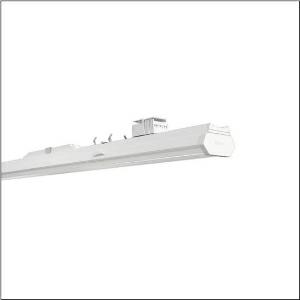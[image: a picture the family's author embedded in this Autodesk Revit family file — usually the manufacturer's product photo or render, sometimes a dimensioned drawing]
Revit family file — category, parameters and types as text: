
# Revit family: licross_r__21_protected_ho_52tp11dn4axs_b31d
name_source: partatom
category: Lighting Fixtures
units: mm (PartAtom-declared; Revit-internal decimal feet)

## family parameters
Cut with Voids When Loaded = No
Host = Face
Light Source = No
Part Type = Normal
Room Calculation Point = No
Round Connector Dimension = Use Diameter
Shared = No

## types (1)
- --- (1 x LED, 10000 lm, 55.1 W, 4000K)
    Apparent Load = 55 VA
    CIE Flux Codes = 84 94 98 99 100
    Color Rendering = 80
    Color Temperature = 4000K
    Default Elevation = 1800 mm
    Description = Licross® 21 Protected HO, luminaire insert, of sheet steel, galvanised, coil coated, white, length: 1.500mm, width: 90mm, height: 103mm, LED rated luminous flux: 10.000lm, light colour: 840, control gear: DALI 2, with plug, 5-pole, with phase selection, mains connection: 220..240V, AC, 50/60Hz, rated input power: 55W, internal wiring halogen-free, primary light control with lens, of plastic, primary optical cover: cover, of PMMA, light emission: direct distribution, primary light characteristic: symmetric, protection rating (complete): IP64, insulation class (complete): insulation class I (protective earthing), certification: CE, ENEC, VDE, UKCA, protection symbol: D if used in an environment with conductive dust loads with corresponding accessories, impact resistance: IK06, permissible ambient temperature for indoor applications: -25..+45°C, corresponds to IFS (International Featured Standards) requirements for safety and quality in the food industry, reducing of maximum allowable ambient temperature of 5°C with ceiling mounting, LABS conformity tested according to VDMA 24364:2018-05, packaging unit: 1 piece
    Height = 92 mm
    Lamp = 1 x LED
    Lamp Light Flux = 10000 lm
    Lamp Power = 55.1 W
    Lamp count = 1
    Length = 1500 mm
    Luminous efficacy = 181 lm/W
    Manufacturer = Siteco
    ModVariant = No
    Model = 52TP11DN4AXS
    Mounting Place = Ceiling
    Mounting Type = Pendant
    Number of Poles = 1
    OnlyDefault = Yes
    Power Factor = 1
    Product Name = Licross® 21 Protected HO
    Product group = luminaire insert | ceiling pendant
    ProductGroupID = 902
    Protection Class = Protection class I
    Protection Degree = IP 64
    RLX_Detail_Level = 1
    RLX_Emergency_Light_Flux = 0 lm
    RLX_Emergency_Type = 0
    RLX_Emergency_Type_DB = No
    RlxData = <blob elided: 24233 chars, md5=e0029af5>
    Socket = socket
    Standby Power = 0 W
    System Light Flux = 10000 lm
    System Power = 55 W
    Type Comments = factory setting: luminous flux: 100 % | dim-lin: 254 | 316 mA
    Type Image = l_1256148.jpg
    URL = http://relux.com
    VarID = @adj_149905
    Voltage = 0 V
    Weight = 0.00 kg
    Width = 88 mm

## geometry (parser evidence)
native form markers: Blend x4, Sweep x10
no freeform markers — native parametric forms only
